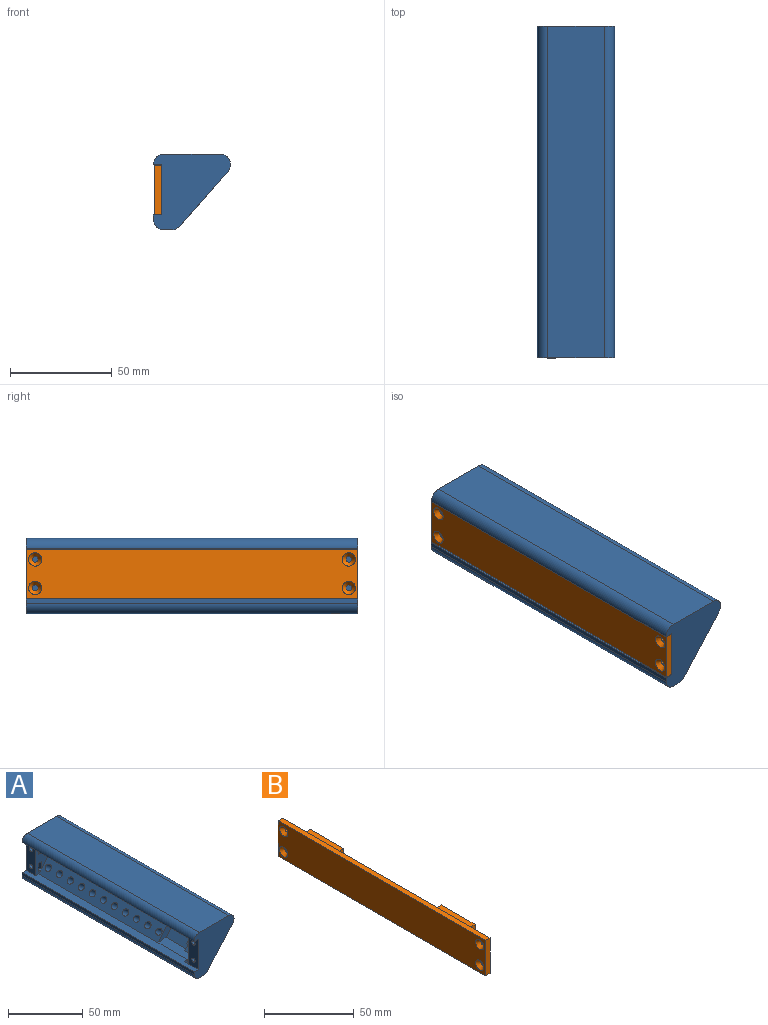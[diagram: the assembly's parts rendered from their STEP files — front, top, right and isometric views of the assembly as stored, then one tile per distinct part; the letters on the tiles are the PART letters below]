
ASSEMBLY  parts=2 mates=1
PART A: 118 faces, bbox 37.9x163.3x37.1 mm
  f0: plane 12.5x3.72mm, normal (-0.75,0,0.66), area 62mm2, adj f9,f33,f34,f79
  f1: cylinder r=4mm len=8mm, axis (-0.75,0,0.66), area 62.8mm2, adj f26,f113
  f2: plane 3.62x3.44mm, normal (0,-1,0), area 5.3mm2, adj f3,f5,f113,f114
  f3: plane 2x1.12mm, normal (0.66,0,0.75), area 3mm2, adj f2,f4,f113,f114
  f4: plane 3.62x3.44mm, normal (0,1,0), area 5.3mm2, adj f3,f5,f113,f114
  f5: plane 2x1.12mm, normal (-0.66,0,-0.75), area 3mm2, adj f2,f4,f113,f114
  f6: plane 163.25x4mm, normal (0,0,-1), area 645mm2, adj f9,f25,f81,f82,f111,f115,f116
  f7: plane 24.85x9mm, normal (-1,0,0), area 209.5mm2, adj f9,f28,f30,f82,f98,f99
  f8: plane 24.85x9mm, normal (-1,0,0), area 209.5mm2, adj f16,f28,f30,f81,f100,f101
  f9: plane 34.12x27.05mm, normal (0,1,0), area 466.8mm2, adj f0,f6,f7,f29,f30,f31,f32,f34
  f10: plane 3.25x3mm, normal (0,1,0), area 9.8mm2, adj f11,f12,f83,f97
  f11: plane 3x2.81mm, normal (0,0.5,-0.87), area 9.8mm2, adj f10,f83,f96,f97
  f12: plane 3x2.81mm, normal (0,0.5,0.87), area 9.8mm2, adj f10,f83,f95,f97
  f13: plane 3x2.81mm, normal (0,0.5,0.87), area 9.8mm2, adj f14,f84,f92,f94
  f14: plane 3.25x3mm, normal (0,1,0), area 9.8mm2, adj f13,f15,f84,f94
  f15: plane 3x2.81mm, normal (0,0.5,-0.87), area 9.8mm2, adj f14,f84,f93,f94
  f16: plane 26.85x26.69mm, normal (0,-1,0), area 353mm2, adj f8,f20,f24,f28,f29,f30,f36,f38
  f17: plane 3x2.81mm, normal (0,-0.5,-0.87), area 9.8mm2, adj f18,f20,f89,f90
  f18: plane 3.25x3mm, normal (0,-1,0), area 9.8mm2, adj f17,f19,f20,f89
  f19: plane 3x2.81mm, normal (0,-0.5,0.87), area 9.8mm2, adj f18,f20,f89,f91
  f20: plane 7.31x6.5mm, normal (-1,0,0), area 35.9mm2, adj f16,f17,f18,f19,f88,f90,f91,f108
  f21: plane 3.25x3mm, normal (0,-1,0), area 9.8mm2, adj f22,f23,f24,f85
  f22: plane 3x2.81mm, normal (0,-0.5,0.87), area 9.8mm2, adj f21,f24,f85,f87
  f23: plane 3x2.81mm, normal (0,-0.5,-0.87), area 9.8mm2, adj f21,f24,f85,f86
  f24: plane 7.31x6.5mm, normal (-1,0,0), area 35.9mm2, adj f16,f21,f22,f23,f86,f87,f106
  f25: cylinder r=5mm len=163.25mm, axis (0,1,0), area 692mm2, adj f6,f26,f81,f82
  f26: plane 163.25x27.12mm, normal (0.75,0,-0.66), area 5172.8mm2, adj f1,f25,f35,f37,f39,f40,f41,f42
  f27: plane 163.25x27.93mm, normal (0,0,1), area 4559.4mm2, adj f37,f81,f82,f112
  f28: plane 163.25x7mm, normal (0,0,1), area 1076.8mm2, adj f7,f8,f16,f36,f79,f81,f82,f110
  f29: cylinder r=2mm len=145.25mm, axis (0,-1,0), area 456.3mm2, adj f9,f16,f30,f38
  f30: plane 163.25x7mm, normal (0,0,-1), area 1088.7mm2, adj f7,f8,f9,f16,f29,f81,f82,f112
  f31: plane 12.5x4.01mm, normal (-0.75,0,0.66), area 66.9mm2, adj f9,f32,f33,f80
  f32: plane 12.5x1.5mm, normal (0.66,0,0.75), area 25mm2, adj f9,f31,f33,f78
  f33: plane 20.85x18.53mm, normal (0,1,0), area 74.5mm2, adj f0,f31,f32,f34,f78,f79,f80,f113
  f34: plane 12.5x1.5mm, normal (-0.66,0,-0.75), area 25mm2, adj f0,f9,f33,f78
  f35: cylinder r=3.25mm len=7.52mm, axis (-0.75,0,0.66), area 81.7mm2, adj f26,f77
  f36: plane 113x26.85mm, normal (-0.75,0,0.66), area 3398.6mm2, adj f16,f28,f38,f39,f40,f41,f42,f43
  f37: cylinder r=5mm len=163.25mm, axis (0,-1,0), area 1872.3mm2, adj f26,f27,f81,f82
  f38: plane 145.25x21.69mm, normal (0,0,-1), area 3150.9mm2, adj f9,f16,f29,f36,f80
  f39: cylinder r=2.5mm len=9.31mm, axis (0.75,0,-0.66), area 125.7mm2, adj f26,f36
  f40: cylinder r=2.5mm len=9.31mm, axis (0.75,0,-0.66), area 125.7mm2, adj f26,f36
  f41: cylinder r=2.5mm len=9.31mm, axis (0.75,0,-0.66), area 125.7mm2, adj f26,f36
  f42: cylinder r=2.5mm len=9.31mm, axis (0.75,0,-0.66), area 125.7mm2, adj f26,f36
  f43: cylinder r=2.5mm len=9.31mm, axis (0.75,0,-0.66), area 125.7mm2, adj f26,f36
  f44: cylinder r=2.5mm len=9.31mm, axis (0.75,0,-0.66), area 125.7mm2, adj f26,f36
  f45: cylinder r=2.5mm len=9.31mm, axis (0.75,0,-0.66), area 125.7mm2, adj f26,f36
  f46: cylinder r=2.5mm len=9.31mm, axis (0.75,0,-0.66), area 125.7mm2, adj f26,f36
  f47: cylinder r=2.5mm len=9.31mm, axis (0.75,0,-0.66), area 125.7mm2, adj f26,f36
  f48: cylinder r=2.5mm len=9.31mm, axis (0.75,0,-0.66), area 125.7mm2, adj f26,f36
  f49: cylinder r=2.5mm len=9.31mm, axis (0.75,0,-0.66), area 125.7mm2, adj f26,f36
  f50: cylinder r=2.5mm len=9.31mm, axis (0.75,0,-0.66), area 125.7mm2, adj f26,f36
  f51: cylinder r=2.5mm len=9.31mm, axis (0.75,0,-0.66), area 125.7mm2, adj f26,f36
  f52: cylinder r=2.5mm len=9.31mm, axis (0.75,0,-0.66), area 125.7mm2, adj f26,f36
  f53: cylinder r=2.5mm len=9.31mm, axis (0.75,0,-0.66), area 125.7mm2, adj f26,f36
  f54: cylinder r=2.5mm len=9.31mm, axis (0.75,0,-0.66), area 125.7mm2, adj f26,f36
  f55: cylinder r=2.5mm len=9.31mm, axis (0.75,0,-0.66), area 125.7mm2, adj f26,f36
  f56: cylinder r=2.5mm len=9.31mm, axis (0.75,0,-0.66), area 125.7mm2, adj f26,f36
  f57: cylinder r=2.5mm len=9.31mm, axis (0.75,0,-0.66), area 125.7mm2, adj f26,f36
  f58: cylinder r=2.5mm len=9.31mm, axis (0.75,0,-0.66), area 125.7mm2, adj f26,f36
  f59: cylinder r=2.5mm len=9.31mm, axis (0.75,0,-0.66), area 125.7mm2, adj f26,f36
  f60: cylinder r=2.5mm len=9.31mm, axis (0.75,0,-0.66), area 125.7mm2, adj f26,f36
  f61: cylinder r=2.5mm len=9.31mm, axis (0.75,0,-0.66), area 125.7mm2, adj f26,f36
  f62: cylinder r=2.5mm len=9.31mm, axis (0.75,0,-0.66), area 125.7mm2, adj f26,f36
  f63: cylinder r=2.5mm len=9.31mm, axis (0.75,0,-0.66), area 125.7mm2, adj f26,f36
  f64: cylinder r=2.5mm len=9.31mm, axis (0.75,0,-0.66), area 125.7mm2, adj f26,f36
  f65: cylinder r=2.5mm len=9.31mm, axis (0.75,0,-0.66), area 125.7mm2, adj f26,f36
  f66: cylinder r=2.5mm len=9.31mm, axis (0.75,0,-0.66), area 125.7mm2, adj f26,f36
  f67: cylinder r=2.5mm len=9.31mm, axis (0.75,0,-0.66), area 125.7mm2, adj f26,f36
  f68: cylinder r=2.5mm len=9.31mm, axis (0.75,0,-0.66), area 125.7mm2, adj f26,f36
  f69: cylinder r=2.5mm len=9.31mm, axis (0.75,0,-0.66), area 125.7mm2, adj f26,f36
  f70: cylinder r=2.5mm len=9.31mm, axis (0.75,0,-0.66), area 125.7mm2, adj f26,f36
  f71: cylinder r=2.5mm len=9.31mm, axis (0.75,0,-0.66), area 125.7mm2, adj f26,f36
  f72: plane 26.85x24.18mm, normal (0,-1,0), area 166.7mm2, adj f36,f79,f80,f113
  f73: plane 11.45x10.43mm, normal (0,1,0), area 27mm2, adj f74,f76,f77,f78
  f74: plane 8.5x1.5mm, normal (-0.66,0,-0.75), area 17mm2, adj f73,f75,f77,f78
  f75: plane 11.45x10.43mm, normal (0,-1,0), area 27mm2, adj f74,f76,f77,f78
  f76: plane 8.5x1.5mm, normal (0.66,0,0.75), area 17mm2, adj f73,f75,f77,f78
  f77: plane 10.12x8.93mm, normal (-0.75,0,0.66), area 81.6mm2, adj f35,f73,f74,f75,f76
  f78: plane 13.12x12.5mm, normal (-0.75,0,0.66), area 104mm2, adj f9,f32,f33,f34,f73,f74,f75,f76
  f79: plane 32.25x7.76mm, normal (-0.06,0,1), area 224.3mm2, adj f0,f9,f28,f33,f72,f113,f115
  f80: plane 32.25x7.76mm, normal (-1,0,-0.06), area 224.3mm2, adj f9,f31,f33,f38,f72,f113
  f81: plane 37.93x37.12mm, normal (0,1,0), area 888.2mm2, adj f6,f8,f25,f26,f27,f28,f30,f37
  f82: plane 37.93x37.12mm, normal (0,-1,0), area 888.2mm2, adj f6,f7,f25,f26,f27,f28,f30,f37
  f83: plane 7.31x6.5mm, normal (-1,0,0), area 35.9mm2, adj f9,f10,f11,f12,f95,f96,f104
  f84: plane 7.31x6.5mm, normal (-1,0,0), area 35.9mm2, adj f9,f13,f14,f15,f92,f93,f102
  f85: plane 7.31x6.5mm, normal (1,0,0), area 35.9mm2, adj f16,f21,f22,f23,f86,f87,f101
  f86: plane 4.5x3mm, normal (0,0,-1), area 13.5mm2, adj f16,f23,f24,f85
  f87: plane 4.5x3mm, normal (0,0,1), area 13.5mm2, adj f16,f22,f24,f85
  f88: plane 0.66x0.58mm, normal (0,1,0), area 0.2mm2, adj f20,f36,f91
  f89: plane 7.31x6.5mm, normal (1,0,0), area 35.9mm2, adj f16,f17,f18,f19,f90,f91,f100
  f90: plane 4.5x3mm, normal (0,0,-1), area 13.5mm2, adj f16,f17,f20,f89
  f91: plane 4.5x3mm, normal (0,0,1), area 13.5mm2, adj f16,f19,f20,f88,f89
  f92: plane 4.5x3mm, normal (0,0,1), area 13.5mm2, adj f9,f13,f84,f94
  f93: plane 4.5x3mm, normal (0,0,-1), area 13.5mm2, adj f9,f15,f84,f94
  f94: plane 7.31x6.5mm, normal (1,0,0), area 35.9mm2, adj f9,f13,f14,f15,f92,f93,f99
  f95: plane 4.5x3mm, normal (0,0,1), area 13.5mm2, adj f9,f12,f83,f97
  f96: plane 4.5x3mm, normal (0,0,-1), area 13.5mm2, adj f9,f11,f83,f97
  f97: plane 7.31x6.5mm, normal (1,0,0), area 35.9mm2, adj f9,f10,f11,f12,f95,f96,f98
  f98: cylinder r=1.5mm len=3mm, axis (-1,0,0), area 23.6mm2, adj f7,f97
  f99: cylinder r=1.5mm len=3mm, axis (-1,0,0), area 23.6mm2, adj f7,f94
  f100: cylinder r=1.5mm len=3mm, axis (-1,0,0), area 23.6mm2, adj f8,f89
  f101: cylinder r=1.5mm len=3mm, axis (-1,0,0), area 23.6mm2, adj f8,f85
  f102: cylinder r=1.5mm len=4.5mm, axis (-1,0,0), area 42.4mm2, adj f84,f103
  f103: plane 3x3mm, normal (-1,0,0), area 7.1mm2, adj f102
  f104: cylinder r=1.5mm len=4.5mm, axis (-1,0,0), area 42.4mm2, adj f83,f105
  f105: plane 3x3mm, normal (-1,0,0), area 7.1mm2, adj f104
  f106: cylinder r=1.5mm len=4.5mm, axis (-1,0,0), area 42.4mm2, adj f24,f107
  f107: plane 3x3mm, normal (-1,0,0), area 7.1mm2, adj f106
  f108: cylinder r=1.5mm len=4.5mm, axis (-1,0,0), area 42.4mm2, adj f20,f109
  f109: plane 3x3mm, normal (-1,0,0), area 7.1mm2, adj f108
  f110: plane 163.25x2.27mm, normal (-1,0,0), area 370.2mm2, adj f28,f81,f82,f111
  f111: cylinder r=5mm len=163.25mm, axis (0,-1,0), area 1278.1mm2, adj f6,f9,f81,f82,f110,f116,f117
  f112: cylinder r=5mm len=163.25mm, axis (0,1,0), area 1282.2mm2, adj f27,f30,f81,f82
  f113: plane 19.75x18.6mm, normal (-0.75,0,0.66), area 432.7mm2, adj f1,f2,f3,f4,f5,f33,f72,f79
  f114: plane 2.62x2.32mm, normal (-0.75,0,0.66), area 7mm2, adj f2,f3,f4,f5
  f115: plane 7.27x4mm, normal (-1,0,0), area 29.1mm2, adj f6,f9,f79,f116
  f116: plane 7.27x3mm, normal (0,-1,0), area 21.8mm2, adj f6,f28,f111,f115,f117
  f117: plane 7.17x4mm, normal (1,0,0), area 28.7mm2, adj f9,f28,f111,f116
PART B: 34 faces, bbox 8.6x163.3x24.2 mm
  f0: plane 163.25x24.2mm, normal (1,0,0), area 3047.9mm2, adj f1,f2,f3,f4,f5,f6,f12,f13
  f1: plane 24.2x3.6mm, normal (0,1,0), area 87.1mm2, adj f0,f7,f12,f13
  f2: plane 24.2x3.6mm, normal (0,-1,0), area 87.1mm2, adj f0,f7,f12,f13
  f3: cylinder r=1.5mm len=3mm, axis (-1,0,0), area 10.4mm2, adj f0,f9
  f4: cylinder r=1.5mm len=3mm, axis (-1,0,0), area 10.4mm2, adj f0,f10
  f5: cylinder r=1.5mm len=3mm, axis (-1,0,0), area 10.4mm2, adj f0,f11
  f6: cylinder r=1.5mm len=3mm, axis (-1,0,0), area 10.4mm2, adj f0,f8
  f7: plane 163.25x24.2mm, normal (-1,0,0), area 3817.9mm2, adj f1,f2,f8,f9,f10,f11,f12,f13
  f8: cone r=3.25mm half-angle=35deg, axis (-1,0,0), area 45.5mm2, adj f6,f7
  f9: cone r=3.25mm half-angle=35deg, axis (-1,0,0), area 45.5mm2, adj f3,f7
  f10: cone r=3.25mm half-angle=35deg, axis (-1,0,0), area 45.5mm2, adj f4,f7
  f11: cone r=3.25mm half-angle=35deg, axis (-1,0,0), area 45.5mm2, adj f5,f7
  f12: plane 163.25x3.6mm, normal (0,0,1), area 587.7mm2, adj f0,f1,f2,f7
  f13: plane 163.25x3.6mm, normal (0,0,-1), area 587.7mm2, adj f0,f1,f2,f7
  f14: plane 16.5x5mm, normal (0,1,0), area 82.5mm2, adj f0,f15,f21,f22
  f15: plane 26.5x5mm, normal (0,0,1), area 132.5mm2, adj f0,f14,f16,f22
  f16: plane 16.5x5mm, normal (0,-1,0), area 82.5mm2, adj f0,f15,f21,f22
  f17: plane 10.5x5mm, normal (0,-1,0), area 52.5mm2, adj f18,f20,f22,f23
  f18: plane 20.5x5mm, normal (0,0,1), area 102.5mm2, adj f17,f19,f22,f23
  f19: plane 10.5x5mm, normal (0,1,0), area 52.5mm2, adj f18,f20,f22,f23
  f20: plane 20.5x5mm, normal (0,0,-1), area 102.5mm2, adj f17,f19,f22,f23
  f21: plane 26.5x5mm, normal (0,0,-1), area 132.5mm2, adj f0,f14,f16,f22
  f22: plane 26.5x16.5mm, normal (1,0,0), area 222mm2, adj f14,f15,f16,f17,f18,f19,f20,f21
  f23: plane 20.5x10.5mm, normal (1,0,0), area 215.3mm2, adj f17,f18,f19,f20
  f24: plane 20.5x5mm, normal (0,0,1), area 102.5mm2, adj f25,f31,f32,f33
  f25: plane 10.5x5mm, normal (0,1,0), area 52.5mm2, adj f24,f26,f32,f33
  f26: plane 20.5x5mm, normal (0,0,-1), area 102.5mm2, adj f25,f31,f32,f33
  f27: plane 26.5x5mm, normal (0,0,1), area 132.5mm2, adj f0,f28,f30,f32
  f28: plane 16.5x5mm, normal (0,-1,0), area 82.5mm2, adj f0,f27,f29,f32
  f29: plane 26.5x5mm, normal (0,0,-1), area 132.5mm2, adj f0,f28,f30,f32
  f30: plane 16.5x5mm, normal (0,1,0), area 82.5mm2, adj f0,f27,f29,f32
  f31: plane 10.5x5mm, normal (0,-1,0), area 52.5mm2, adj f24,f26,f32,f33
  f32: plane 26.5x16.5mm, normal (1,0,0), area 222mm2, adj f24,f25,f26,f27,f28,f29,f30,f31
  f33: plane 20.5x10.5mm, normal (1,0,0), area 215.2mm2, adj f24,f25,f26,f31
PLACE A t=(-31.79,33.55,-46.99)mm
PLACE B t=(-50.39,35.05,16.9)mm
MATE fastened B.f3 <-> A.f101  axis (1,0,0) through (-46.79,35.05,-27.42)mm
